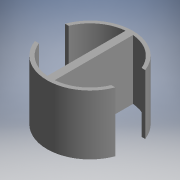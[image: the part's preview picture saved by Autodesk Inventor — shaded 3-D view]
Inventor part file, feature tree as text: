
AUTODESK INVENTOR PART (.ipt)
format: ipt  version: 2018 (Build 220112000, 112)  size: 97,792 bytes
history: native  units: mm (DEFAULTED — no unit token found)
features: extrude x1, sketch x1
ambient origin geometry x8: Origin, YZ Plane, XZ Plane, XY Plane, X Axis, Y Axis, Z Axis, Center Point
bodies: Solid1 (feature_tree)
feature tree (2):
  extrude  "Extrusion1"  Depth=50.8mm TaperAngle=0.0deg
  sketch  "Sketch1"  dims[d0=28.75mm d1=26.25mm d2=5.0mm d3=10.0mm d5=50.8mm d6=0.0mm d9=73.025mm d10=66.675mm d11=25.4mm d13=12.7mm d14=3.175mm d16=3.175mm d17=3.175mm]
